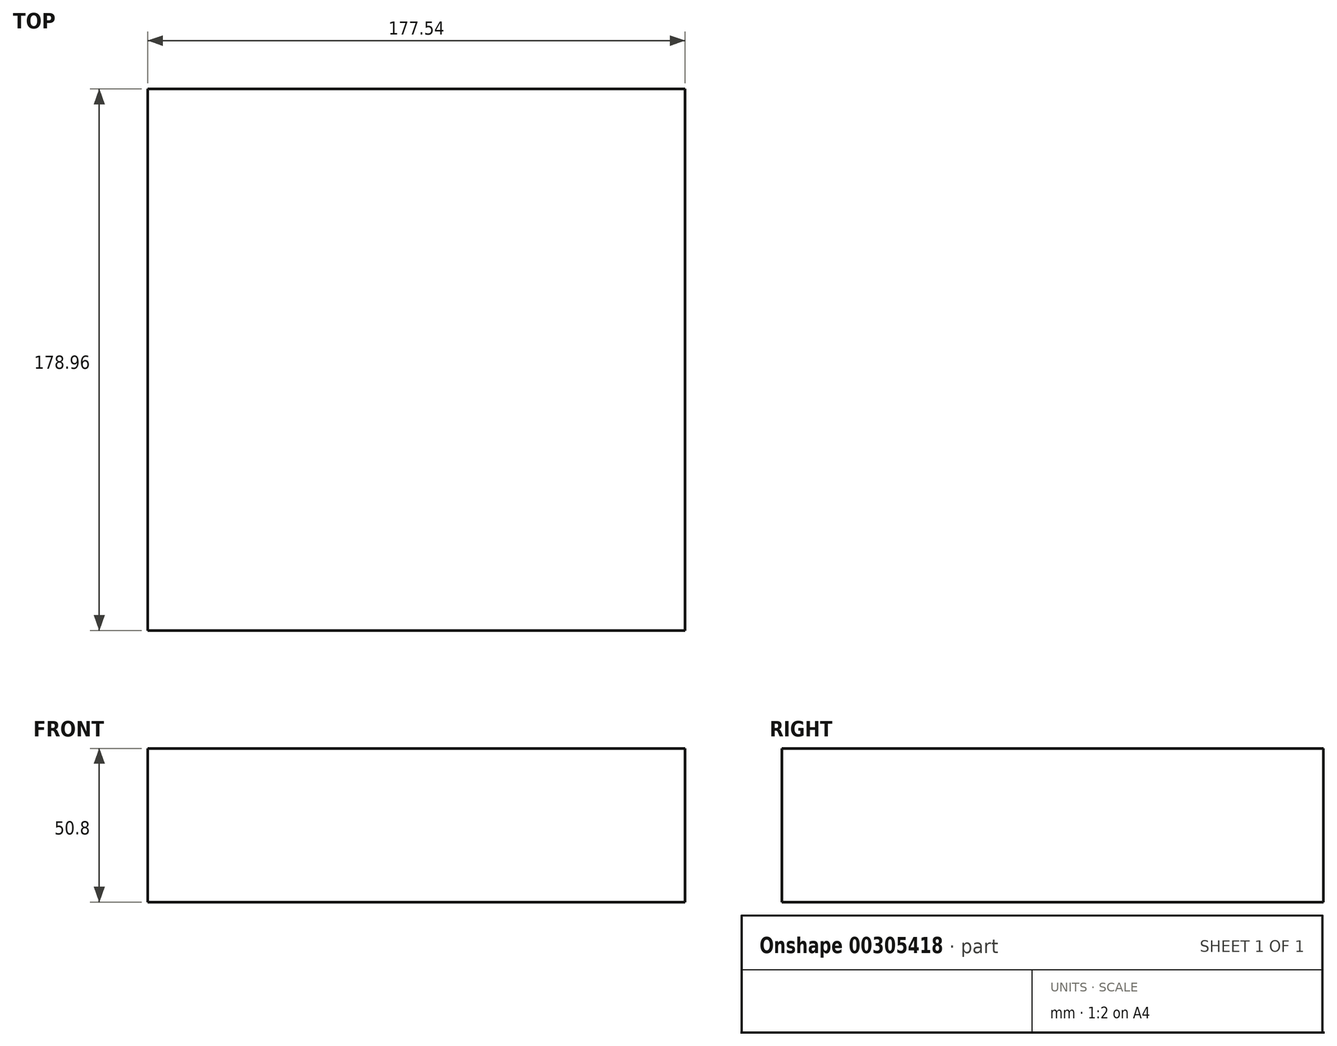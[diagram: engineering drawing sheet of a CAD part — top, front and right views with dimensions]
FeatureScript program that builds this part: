
annotation { "Feature Type Name" : "Feature", "Feature Type Description" : "" }
export const myFeature = defineFeature(function(context is Context, id is Id, definition is map)
    precondition{}
    {
        {
            var Q0;
            Q0=qCreatedBy(makeId("Top.planeOp"),FACE);
            var sketch = newSketch(context, id + "F0", { "sketchPlane" : qUnion([Q0])});
            skLineSegment(sketch, "E0.bottom", {"start": v(88.77, -89.48) * mm, "end": v(-88.77, -89.48) * mm});
            skLineSegment(sketch, "E0.top", {"start": v(88.77, 89.48) * mm, "end": v(-88.77, 89.48) * mm});
            skLineSegment(sketch, "E0.left", {"start": v(88.77, -89.48) * mm, "end": v(88.77, 89.48) * mm});
            skLineSegment(sketch, "E0.right", {"start": v(-88.77, -89.48) * mm, "end": v(-88.77, 89.48) * mm});
            skPoint(sketch, "E0.middle", {"position": v(0, 0) * mm});
            skSolve(sketch);
        }
        {
            var Q0;
            Q0 = qSketchRegion(id + "F0", true);
            extrude(context, id + "F1", {"entities" : qUnion([Q0]), "depth" : 50.8 * mm});
        }
    });
